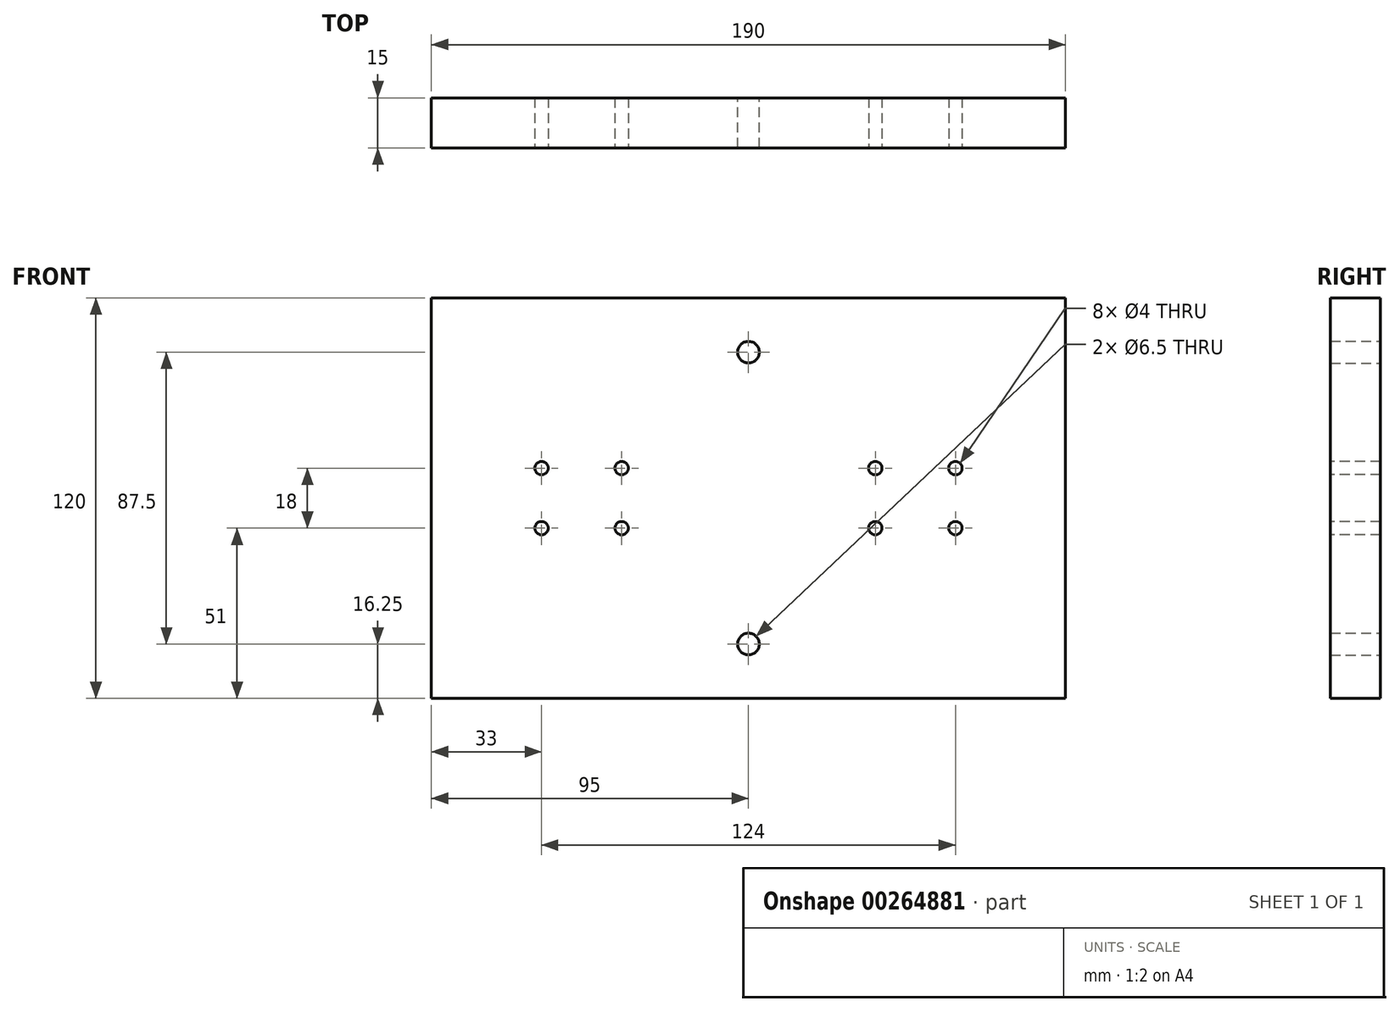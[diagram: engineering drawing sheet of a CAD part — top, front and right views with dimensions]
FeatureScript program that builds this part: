
annotation { "Feature Type Name" : "Feature", "Feature Type Description" : "" }
export const myFeature = defineFeature(function(context is Context, id is Id, definition is map)
    precondition{}
    {
        {
            var Q0;
            Q0=qCreatedBy(makeId("Top.planeOp"),FACE);
            var sketch = newSketch(context, id + "F0", { "sketchPlane" : qUnion([Q0])});
            skLineSegment(sketch, "E0.bottom", {"start": v(95, -7.5) * mm, "end": v(-95, -7.5) * mm});
            skLineSegment(sketch, "E0.top", {"start": v(95, 7.5) * mm, "end": v(-95, 7.5) * mm});
            skLineSegment(sketch, "E0.left", {"start": v(95, -7.5) * mm, "end": v(95, 7.5) * mm});
            skLineSegment(sketch, "E0.right", {"start": v(-95, -7.5) * mm, "end": v(-95, 7.5) * mm});
            skPoint(sketch, "E0.middle", {"position": v(0, 0) * mm});
            skSolve(sketch);
        }
        {
            var Q0;
            Q0 = qSketchRegion(id + "F0", true);
            extrude(context, id + "F1", {"entities" : qUnion([Q0]), "depth" : 120 * mm});
        }
        {
            var Q0;
            Q0=makeQuery(id+"F1.opExtrude","SWEPT_FACE",FACE,{"disambiguationData":[OSD([sQuery(id+"F0.wireOp",EDGE,"E0.bottom")])]});
            var sketch = newSketch(context, id + "F2", { "sketchPlane" : qUnion([Q0])});
            skCircle(sketch, "E1", {"center": v(-62, 69) * mm, "radius": 2 * mm});
            skCircle(sketch, "E2", {"center": v(-161.05, -20.15) * mm, "radius": 0.9 * mm});
            skCircle(sketch, "E3", {"center": v(-164.95, -26.28) * mm, "radius": 1.11 * mm});
            skCircle(sketch, "E4", {"center": v(-381.15, -111.37) * mm, "radius": 1 * mm});
            skCircle(sketch, "E5", {"center": v(-38, 69) * mm, "radius": 2 * mm});
            skCircle(sketch, "E6", {"center": v(-62, 51) * mm, "radius": 2 * mm});
            skCircle(sketch, "E7", {"center": v(-38, 51) * mm, "radius": 2 * mm});
            skCircle(sketch, "E8", {"center": v(38, 51) * mm, "radius": 2 * mm});
            skCircle(sketch, "E9", {"center": v(62, 51) * mm, "radius": 2 * mm});
            skCircle(sketch, "E10", {"center": v(38, 69) * mm, "radius": 2 * mm});
            skCircle(sketch, "E11", {"center": v(62, 69) * mm, "radius": 2 * mm});
            skSolve(sketch);
        }
        {
            var Q0;
            Q0 = qSketchRegion(id + "F2", true);
            extrude(context, id + "F3", {"entities" : qUnion([Q0]), "operationType" : NewBodyOperationType.REMOVE, "endBound" : BoundingType.THROUGH_ALL, "oppositeDirection" : true, "depth" : 25.4 * mm});
        }
        {
            var Q0;
            Q0=makeQuery(id+"F1.opExtrude","SWEPT_FACE",FACE,{"disambiguationData":[OSD([sQuery(id+"F0.wireOp",EDGE,"E0.top")])]});
            var sketch = newSketch(context, id + "F4", { "sketchPlane" : qUnion([Q0])});
            skCircle(sketch, "E12", {"center": v(0, 103.75) * mm, "radius": 3.25 * mm});
            skCircle(sketch, "E13", {"center": v(0, 16.25) * mm, "radius": 3.25 * mm});
            skSolve(sketch);
        }
        {
            var Q0;
            Q0 = qSketchRegion(id + "F4", true);
            extrude(context, id + "F5", {"entities" : qUnion([Q0]), "operationType" : NewBodyOperationType.REMOVE, "endBound" : BoundingType.THROUGH_ALL, "oppositeDirection" : true, "depth" : 25.4 * mm});
        }
    });
